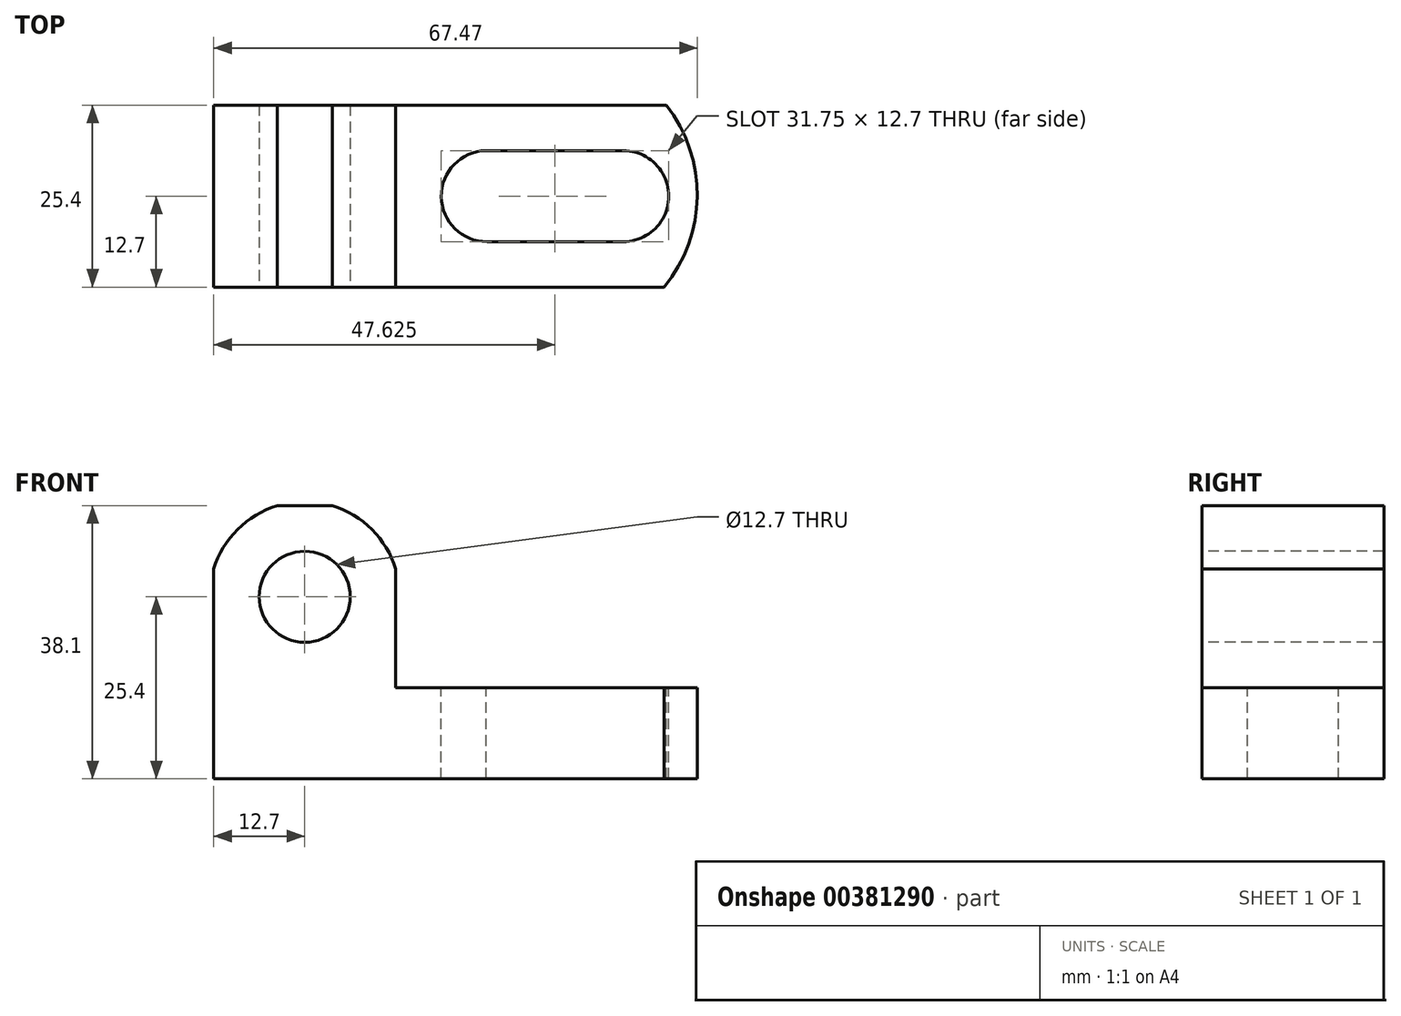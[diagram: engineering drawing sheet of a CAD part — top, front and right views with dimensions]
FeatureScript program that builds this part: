
annotation { "Feature Type Name" : "Feature", "Feature Type Description" : "" }
export const myFeature = defineFeature(function(context is Context, id is Id, definition is map)
    precondition{}
    {
        {
            var Q0;
            Q0=qCreatedBy(makeId("Front.planeOp"),FACE);
            var sketch = newSketch(context, id + "F0", { "sketchPlane" : qUnion([Q0])});
            skLineSegment(sketch, "E0", {"start": v(0, 0) * mm, "end": v(0, 38.1) * mm});
            skLineSegment(sketch, "E1", {"start": v(0, 38.1) * mm, "end": v(25.4, 38.1) * mm});
            skLineSegment(sketch, "E2", {"start": v(25.4, 38.1) * mm, "end": v(25.4, 12.7) * mm});
            skLineSegment(sketch, "E3", {"start": v(25.4, 12.7) * mm, "end": v(69.85, 12.7) * mm});
            skLineSegment(sketch, "E4", {"start": v(69.85, 12.7) * mm, "end": v(69.85, 0) * mm});
            skLineSegment(sketch, "E5", {"start": v(69.85, 0) * mm, "end": v(0, 0) * mm});
            skSolve(sketch);
        }
        {
            var Q0;
            Q0 = qSketchRegion(id + "F0", true);
            extrude(context, id + "F1", {"entities" : qUnion([Q0]), "depth" : 25.4 * mm});
        }
        {
            var Q0;
            Q0=makeQuery(id+"F1.opExtrude","CAP_FACE",FACE,{"disambiguationData":[OSD([sQuery(id+"F0.wireOp",EDGE,"E0"),sQuery(id+"F0.wireOp",EDGE,"E1"),sQuery(id+"F0.wireOp",EDGE,"E2"),sQuery(id+"F0.wireOp",EDGE,"E3"),sQuery(id+"F0.wireOp",EDGE,"E4"),sQuery(id+"F0.wireOp",EDGE,"E5")])],"isStart":false});
            var sketch = newSketch(context, id + "F2", { "sketchPlane" : qUnion([Q0])});
            skCircle(sketch, "E6", {"center": v(12.7, 25.4) * mm, "radius": 6.35 * mm});
            skSolve(sketch);
        }
        {
            var Q0;
            Q0 = qSketchRegion(id + "F2", true);
            extrude(context, id + "F3", {"entities" : qUnion([Q0]), "operationType" : NewBodyOperationType.REMOVE, "oppositeDirection" : true, "depth" : 25.4 * mm});
        }
        {
            var Q0;
            Q0=makeQuery(id+"F1.opExtrude","CAP_FACE",FACE,{"disambiguationData":[OSD([sQuery(id+"F0.wireOp",EDGE,"E0"),sQuery(id+"F0.wireOp",EDGE,"E1"),sQuery(id+"F0.wireOp",EDGE,"E2"),sQuery(id+"F0.wireOp",EDGE,"E3"),sQuery(id+"F0.wireOp",EDGE,"E4"),sQuery(id+"F0.wireOp",EDGE,"E5")])],"isStart":false});
            var sketch = newSketch(context, id + "F4", { "sketchPlane" : qUnion([Q0])});
            skPoint(sketch, "E7.centerSnap0", {"position": v(25.4, 25.4) * mm});
            skCircle(sketch, "E8", {"center": v(12.7, 25.4) * mm, "radius": 13.27 * mm});
            skSolve(sketch);
        }
        {
            var Q0;
            {var subQ0=sQuery(id+"F4.wireOp",EDGE,"E8");var subQ1=makeQuery(id+"F1.opExtrude","CAP_EDGE",EDGE,{"disambiguationData":[OSD([sQuery(id+"F0.wireOp",EDGE,"E1")])],"isStart":false});var subQ2=makeQuery(id+"F4.imprint","INTERSECT",VERTEX,{"disambiguationData":[OD(1.0)],"derivedFrom":[subQ1,subQ0]});Q0=makeQuery(id+"F4.imprint","IMPRINT",FACE,{"disambiguationData":[TD([[makeQuery(id+"F4.imprint","IMPRINT",EDGE,{"disambiguationData":[TD([[subQ2,-1.0]])],"derivedFrom":subQ0}),-1.0]])]});}
            var Q1;
            {var subQ0=sQuery(id+"F4.wireOp",EDGE,"E8");var subQ1=makeQuery(id+"F1.opExtrude","CAP_EDGE",EDGE,{"disambiguationData":[OSD([sQuery(id+"F0.wireOp",EDGE,"E1")])],"isStart":false});var subQ2=makeQuery(id+"F4.imprint","INTERSECT",VERTEX,{"disambiguationData":[OD(0.0)],"derivedFrom":[subQ1,subQ0]});Q1=makeQuery(id+"F4.imprint","IMPRINT",FACE,{"disambiguationData":[TD([[makeQuery(id+"F4.imprint","IMPRINT",EDGE,{"disambiguationData":[TD([[subQ2,1.0]])],"derivedFrom":subQ0}),-1.0]])]});}
            extrude(context, id + "F5", {"entities" : qUnion([Q0, Q1]), "operationType" : NewBodyOperationType.REMOVE, "oppositeDirection" : true, "depth" : 25.4 * mm});
        }
        {
            var Q0;
            Q0=makeQuery(id+"F1.opExtrude","SWEPT_FACE",FACE,{"disambiguationData":[OSD([sQuery(id+"F0.wireOp",EDGE,"E3")])]});
            var sketch = newSketch(context, id + "F6", { "sketchPlane" : qUnion([Q0])});
            skCircle(sketch, "E9", {"center": v(38.1, -12.7) * mm, "radius": 6.35 * mm});
            skCircle(sketch, "E10", {"center": v(57.15, -12.7) * mm, "radius": 6.35 * mm});
            skLineSegment(sketch, "E11", {"start": v(38.15, -19.05) * mm, "end": v(57.15, -19.05) * mm});
            skLineSegment(sketch, "E12", {"start": v(37.99, -6.35) * mm, "end": v(57.15, -6.35) * mm});
            skArc(sketch, "E13", {"start": v(62.83, -25.4) * mm, "mid": v(67.47, -12.75) * mm, "end": v(63.14, 0) * mm});
            skSolve(sketch);
        }
        {
            var Q0;
            {var subQ0=sQuery(id+"F6.wireOp",EDGE,"E9");var subQ1=makeQuery(id+"F6.imprint","INTERSECT",VERTEX,{"derivedFrom":[subQ0,sQuery(id+"F6.wireOp",EDGE,"E11")]});Q0=makeQuery(id+"F6.imprint","IMPRINT",FACE,{"disambiguationData":[TD([[makeQuery(id+"F6.imprint","IMPRINT",EDGE,{"disambiguationData":[TD([[subQ1,1.0]])],"derivedFrom":subQ0}),1.0]])]});}
            var Q1;
            {var subQ0=sQuery(id+"F6.wireOp",EDGE,"E11");Q1=makeQuery(id+"F6.imprint","IMPRINT",FACE,{"disambiguationData":[TD([[makeQuery(id+"F6.imprint","IMPRINT",EDGE,{"derivedFrom":subQ0}),1.0]])]});}
            var Q2;
            {var subQ0=sQuery(id+"F6.wireOp",EDGE,"E10");var subQ1=makeQuery(id+"F6.imprint","INTERSECT",VERTEX,{"derivedFrom":[subQ0,sQuery(id+"F6.wireOp",EDGE,"E11")]});Q2=makeQuery(id+"F6.imprint","IMPRINT",FACE,{"disambiguationData":[TD([[makeQuery(id+"F6.imprint","IMPRINT",EDGE,{"disambiguationData":[TD([[subQ1,1.0]])],"derivedFrom":subQ0}),1.0]])]});}
            var Q3;
            {var subQ0=sQuery(id+"F6.wireOp",EDGE,"E13");Q3=makeQuery(id+"F6.imprint","IMPRINT",FACE,{"disambiguationData":[TD([[makeQuery(id+"F6.imprint","IMPRINT",EDGE,{"derivedFrom":subQ0}),-1.0]])]});}
            extrude(context, id + "F7", {"entities" : qUnion([Q0, Q1, Q2, Q3]), "operationType" : NewBodyOperationType.REMOVE, "oppositeDirection" : true, "depth" : 25.4 * mm});
        }
    });
